# Revit family: SLSM_2FT4FT_3500K4000K
name_source: partatom
category: Lighting Fixtures
units: mm (PartAtom-declared; Revit-internal decimal feet)

## family parameters
Always vertical = Yes
Cut with Voids When Loaded = No
Light Source = Yes
Maintain Annotation Orientation = No
OmniClass Number = 23.80.70.00
OmniClass Title = Lighting
Part Type = Normal
Room Calculation Point = No
Round Connector Dimension = Use Diameter
Shared = No
Work Plane-Based = Yes

## types (8) — shared parameters
CRI = 80
Color Filter = 16777215
Default Elevation = 4' - 0"
Dimming Lamp Color Temperature Shift = <None>
IP Rating = 65
Input Voltage = 120-277V
Lamp = LED
Load Classification = Lighting
Manufacturer = Above All Lighting
Power Factor = 0.9
Tilt Angle = 90.00°
URL = https://abovealllighting.com

## per-type parameters (varying)
| type | Model | Photometric Web File | Wattage Comments |
| SLSM_4IN_2FT_20W_3500K | SLSM4-0620SW1-SM | SLSM4-0620SW1-SM_3500K.IES | 20W |
| SLSM_4IN_4FT_40W_3500K | SLSM4-12SPSW1-SM | SLSM4-12SPSW1-SM_3500K.IES | 40W |
| SLSM_4IN_2FT_20W_4000K | SLSM4-0620SW1-SM | SLSM4-0620SW1-SM_4000K.IES | 20W |
| SLSM_4IN_4FT_40W_4000K | SLSM4-12SPSW1-SM | SLSM4-12SPSW1-SM_4000K.IES | 40W |
| SLSM_6IN_2FT_20W_3500K | SLSM6-0620SW1-SM | SLSM6-0620SW1-SM_3500K.IES | 20W |
| SLSM_6IN_2FT_20W_4000K | SLSM6-0620SW1-SM | SLSM6-0620SW1-SM_4000K.IES | 20W |
| SLSM_6IN_4FT_40W_3500K | SLSM6-12SPSW1-SM | SLSM6-12SPSW1-SM_3500K.IES | 40W |
| SLSM_6IN_4FT_40W_4000K | SLSM6-12SPSW1-SM | SLSM6_12SPSW1_SM_4000K.IES | 40W |

## geometry (parser evidence)
native form markers: Sweep x2
no freeform markers — native parametric forms only
